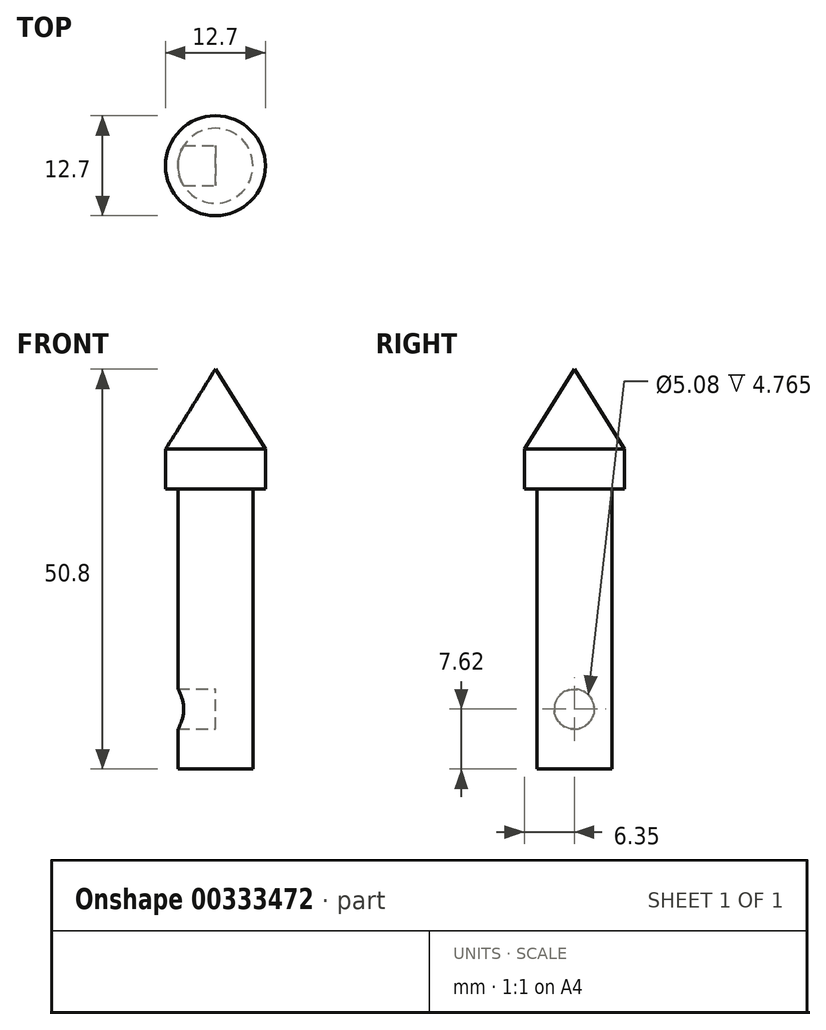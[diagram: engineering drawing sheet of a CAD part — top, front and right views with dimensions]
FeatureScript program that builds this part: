
annotation { "Feature Type Name" : "Feature", "Feature Type Description" : "" }
export const myFeature = defineFeature(function(context is Context, id is Id, definition is map)
    precondition{}
    {
        {
            var Q0;
            Q0=qCreatedBy(makeId("Front.planeOp"),FACE);
            var sketch = newSketch(context, id + "F0", { "sketchPlane" : qUnion([Q0])});
            skLineSegment(sketch, "E0.top", {"start": v(4.76, -25.4) * mm, "end": v(-4.76, -25.4) * mm});
            skLineSegment(sketch, "E0.left", {"start": v(6.35, 15.24) * mm, "end": v(6.35, 10.16) * mm});
            skLineSegment(sketch, "E0.right", {"start": v(-6.35, 15.24) * mm, "end": v(-6.35, 10.16) * mm});
            skPoint(sketch, "E0.middle", {"position": v(0, 0) * mm});
            skLineSegment(sketch, "E1.bottom", {"start": v(-6.35, 15.24) * mm, "end": v(6.35, 15.24) * mm});
            skLineSegment(sketch, "E1.top", {"start": v(-6.35, 10.16) * mm, "end": v(6.35, 10.16) * mm});
            skLineSegment(sketch, "E2.bottom", {"start": v(-4.76, 10.16) * mm, "end": v(4.76, 10.16) * mm});
            skLineSegment(sketch, "E2.top", {"start": v(-4.76, -25.4) * mm, "end": v(4.76, -25.4) * mm});
            skLineSegment(sketch, "E2.left", {"start": v(-4.76, 10.16) * mm, "end": v(-4.76, -25.4) * mm});
            skLineSegment(sketch, "E2.right", {"start": v(4.76, 10.16) * mm, "end": v(4.76, -25.4) * mm});
            skLineSegment(sketch, "E3", {"start": v(-6.35, 15.24) * mm, "end": v(0, 25.4) * mm});
            skLineSegment(sketch, "E4", {"start": v(0, 25.4) * mm, "end": v(6.35, 15.24) * mm});
            skPoint(sketch, "E5.orphan", {"position": v(-6.35, 25.4) * mm});
            skPoint(sketch, "E6.orphan", {"position": v(6.35, 25.4) * mm});
            skPoint(sketch, "E7.orphan", {"position": v(6.35, -25.4) * mm});
            skPoint(sketch, "E8.orphan", {"position": v(-6.35, -25.4) * mm});
            skLineSegment(sketch, "E9", {"start": v(0, 25.4) * mm, "end": v(0, -25.4) * mm});
            skSolve(sketch);
        }
        {
            var Q0;
            {var subQ0=sQuery(id+"F0.wireOp",EDGE,"E4");Q0=makeQuery(id+"F0.imprint","IMPRINT",FACE,{"disambiguationData":[TD([[makeQuery(id+"F0.imprint","IMPRINT",EDGE,{"derivedFrom":subQ0}),-1.0]])]});}
            var Q1;
            {var subQ5=sQuery(id+"F0.wireOp",EDGE,"E0.left");Q1=makeQuery(id+"F0.imprint","IMPRINT",FACE,{"disambiguationData":[TD([[makeQuery(id+"F0.imprint","IMPRINT",EDGE,{"derivedFrom":subQ5}),-1.0]])]});}
            var Q2;
            {var subQ0=sQuery(id+"F0.wireOp",EDGE,"E2.right");Q2=makeQuery(id+"F0.imprint","IMPRINT",FACE,{"disambiguationData":[TD([[makeQuery(id+"F0.imprint","IMPRINT",EDGE,{"derivedFrom":subQ0}),-1.0]])]});}
            var Q3;
            Q3=sQuery(id+"F0.wireOp",EDGE,"E9");
            revolve(context, id + "F1", {"entities" : qUnion([Q0, Q1, Q2]), "axis" : qUnion([Q3]), "revolveType" : RevolveType.FULL});
        }
        {
            var Q0;
            Q0=qCreatedBy(makeId("Right.planeOp"),FACE);
            var sketch = newSketch(context, id + "F2", { "sketchPlane" : qUnion([Q0])});
            skCircle(sketch, "E10", {"center": v(0, -17.78) * mm, "radius": 2.54 * mm});
            skSolve(sketch);
        }
        {
            var Q0;
            Q0 = qSketchRegion(id + "F2", true);
            extrude(context, id + "F3", {"entities" : qUnion([Q0]), "operationType" : NewBodyOperationType.REMOVE, "oppositeDirection" : true, "depth" : 7.62 * mm});
        }
    });
